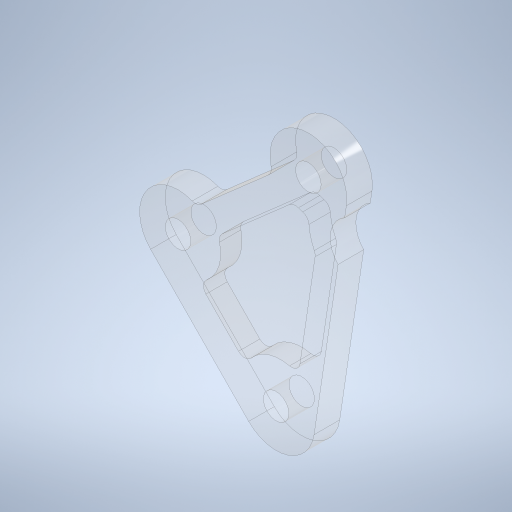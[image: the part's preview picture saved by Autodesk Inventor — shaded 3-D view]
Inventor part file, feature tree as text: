
AUTODESK INVENTOR PART (.ipt)
format: ipt  version: 2023.1 (Build 271208000, 208)  size: 380,928 bytes
history: native  units: mm
features: extrude x5, sketch x5, other x2, fillet x2, projected_geometry x2
ambient origin geometry x8: Origin, YZ Plane, XZ Plane, XY Plane, X Axis, Y Axis, Z Axis, Center Point
bodies: Body1 (feature_tree)
feature tree (16):
  other  "ソリッド1"
  extrude  "押し出し1"  Depth=9.0mm
  extrude  "押し出し2"  Depth=3.0mm TaperAngle=0.0deg
  extrude  "押し出し3"  Depth=9.0mm
  sketch  "スケッチ4"
  extrude  "押し出し4"  Depth=6.5mm
  extrude  "押し出し5"  Depth=10.0mm TaperAngle=0.0deg
  sketch  "スケッチ5"
  fillet  "フィレット1"  Radius=3.0mm
  fillet  "フィレット2"  Radius=2.5mm
  sketch  "スケッチ1"
  sketch  "スケッチ2"
  projected_geometry  "投影ループ1"
  sketch  "スケッチ3"
  projected_geometry  "投影ループ2"
  other  "断面エッジを投影1"
